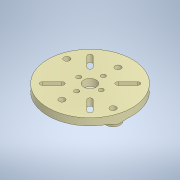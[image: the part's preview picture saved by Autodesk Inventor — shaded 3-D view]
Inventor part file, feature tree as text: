
AUTODESK INVENTOR PART (.ipt)
format: ipt  version: 2021 (Build 250183000, 183)  size: 235,008 bytes
history: native  units: mm
features: extrude x2, sketch x2, other x1, fillet x1, projected_geometry x1
ambient origin geometry x8: Origin, YZ Plane, XZ Plane, XY Plane, X Axis, Y Axis, Z Axis, Center Point
bodies: Body1 (feature_tree)
feature tree (7):
  other  "솔리드1"
  extrude  "돌출1"  Depth=5.0mm TaperAngle=0.0deg
  extrude  "돌출2"  Depth=10.0mm
  fillet  "모깎기1"  Radius=3.0mm
  sketch  "스케치1"
  sketch  "스케치2"
  projected_geometry  "투영된 루프1"
